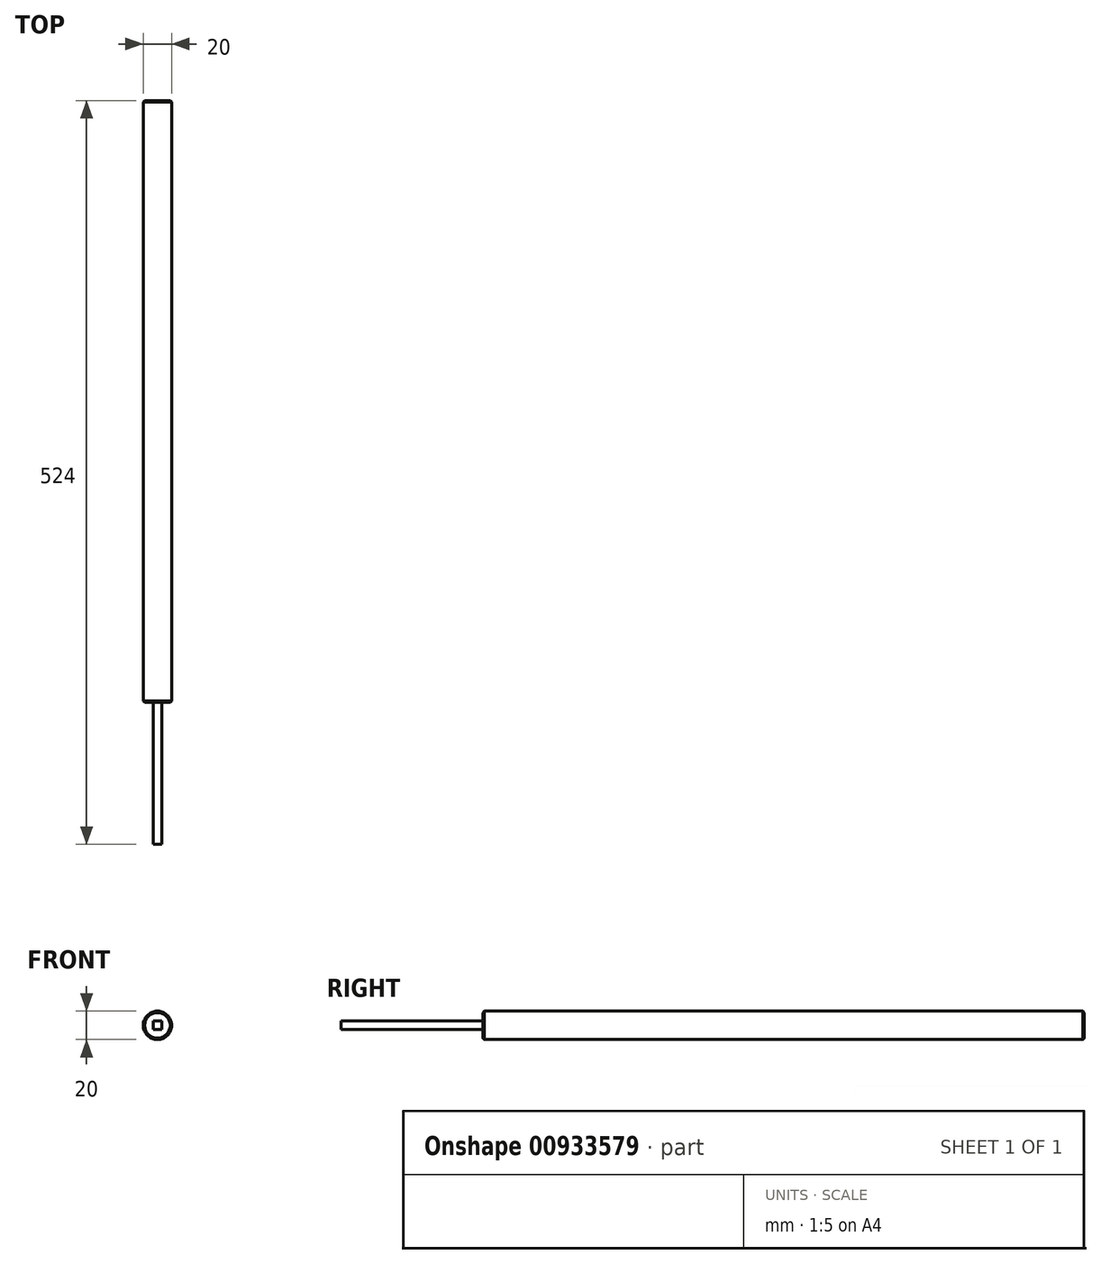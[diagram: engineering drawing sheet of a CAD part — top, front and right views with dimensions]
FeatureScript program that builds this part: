
annotation { "Feature Type Name" : "Feature", "Feature Type Description" : "" }
export const myFeature = defineFeature(function(context is Context, id is Id, definition is map)
    precondition{}
    {
        {
            var Q0;
            Q0=qCreatedBy(makeId("Front.planeOp"),FACE);
            var sketch = newSketch(context, id + "F0", { "sketchPlane" : qUnion([Q0])});
            skCircle(sketch, "E0", {"center": v(0, 0) * mm, "radius": 10 * mm});
            skSolve(sketch);
        }
        {
            var Q0;
            Q0 = qSketchRegion(id + "F0", true);
            extrude(context, id + "F1", {"entities" : qUnion([Q0]), "depth" : 424 * mm, "offsetDistance" : 25 * mm});
        }
        {
            var Q0;
            Q0=makeQuery(id+"F1.opExtrude","CAP_EDGE",EDGE,{"disambiguationData":[OSD([sQuery(id+"F0.wireOp",EDGE,"E0")])],"isStart":true});
            var Q1;
            Q1=makeQuery(id+"F1.opExtrude","CAP_EDGE",EDGE,{"disambiguationData":[OSD([sQuery(id+"F0.wireOp",EDGE,"E0")])],"isStart":false});
            chamfer(context, id + "F2", {"entities" : qUnion([Q0, Q1]), "width" : 1 * mm, "tangentPropagation" : true});
        }
        {
            var Q0;
            Q0=makeQuery(id+"F1.opExtrude","CAP_FACE",FACE,{"disambiguationData":[OSD([sQuery(id+"F0.wireOp",EDGE,"E0")])],"isStart":false});
            var sketch = newSketch(context, id + "F3", { "sketchPlane" : qUnion([Q0])});
            skLineSegment(sketch, "E1.bottom", {"start": v(-3, 3) * mm, "end": v(3, 3) * mm});
            skLineSegment(sketch, "E1.top", {"start": v(-3, -3) * mm, "end": v(3, -3) * mm});
            skLineSegment(sketch, "E1.left", {"start": v(-3, 3) * mm, "end": v(-3, -3) * mm});
            skLineSegment(sketch, "E1.right", {"start": v(3, 3) * mm, "end": v(3, -3) * mm});
            skPoint(sketch, "E1.middle", {"position": v(0, 0) * mm});
            skSolve(sketch);
        }
        {
            var Q0;
            Q0 = qSketchRegion(id + "F3", true);
            extrude(context, id + "F4", {"entities" : qUnion([Q0]), "operationType" : NewBodyOperationType.ADD, "depth" : 100 * mm, "offsetDistance" : 25 * mm});
        }
    });
